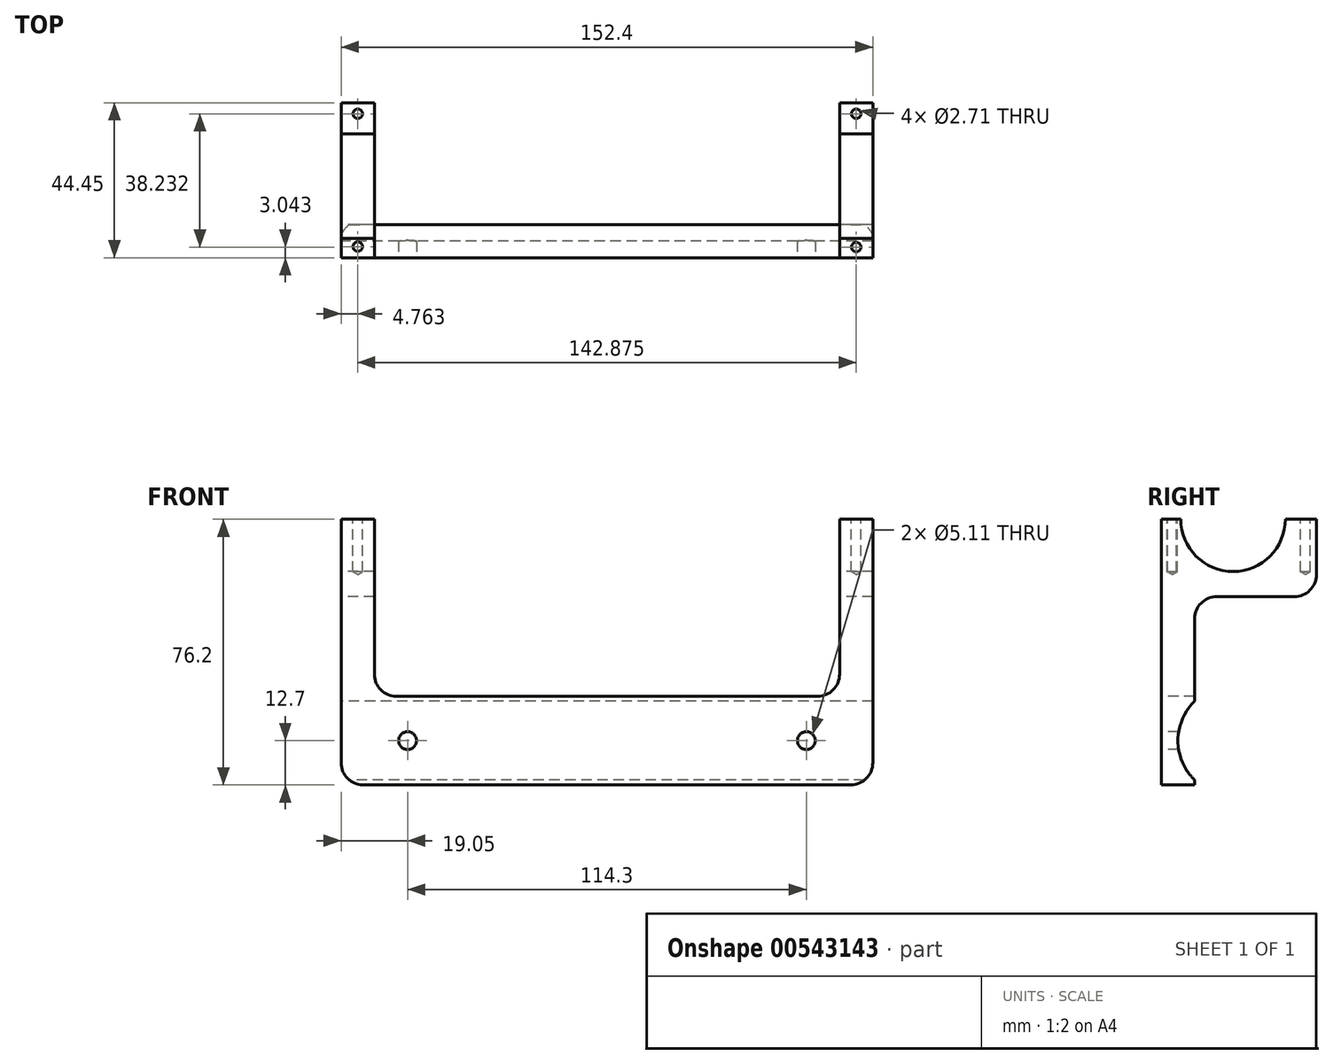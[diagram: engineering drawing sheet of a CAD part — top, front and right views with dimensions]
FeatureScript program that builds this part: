
annotation { "Feature Type Name" : "Feature", "Feature Type Description" : "" }
export const myFeature = defineFeature(function(context is Context, id is Id, definition is map)
    precondition{}
    {
        {
            var Q0;
            Q0=qCreatedBy(makeId("Right.planeOp"),FACE);
            var sketch = newSketch(context, id + "F0", { "sketchPlane" : qUnion([Q0])});
            skLineSegment(sketch, "E0.bottom", {"start": v(-44.45, 76.2) * mm, "end": v(0, 76.2) * mm, "construction": true});
            skLineSegment(sketch, "E0.top", {"start": v(-44.45, 0) * mm, "end": v(0, 0) * mm, "construction": true});
            skLineSegment(sketch, "E0.left", {"start": v(-44.45, 76.2) * mm, "end": v(-44.45, 0) * mm, "construction": true});
            skLineSegment(sketch, "E0.right", {"start": v(0, 76.2) * mm, "end": v(0, 0) * mm, "construction": true});
            skArc(sketch, "E1", {"start": v(-38.9, 76.2) * mm, "mid": v(-23.9, 61.2) * mm, "end": v(-8.9, 76.2) * mm});
            skLineSegment(sketch, "E2", {"start": v(-8.9, 76.2) * mm, "end": v(0, 76.2) * mm});
            skLineSegment(sketch, "E3", {"start": v(0, 53.98) * mm, "end": v(0, 76.2) * mm});
            skLineSegment(sketch, "E4", {"start": v(-38.9, 76.2) * mm, "end": v(-44.45, 76.2) * mm});
            skLineSegment(sketch, "E5", {"start": v(-44.45, 76.2) * mm, "end": v(-44.45, 0) * mm});
            skLineSegment(sketch, "E6", {"start": v(-44.45, 0) * mm, "end": v(-34.93, 0) * mm});
            skLineSegment(sketch, "E7", {"start": v(-34.93, 0) * mm, "end": v(-34.93, 53.98) * mm});
            skLineSegment(sketch, "E8", {"start": v(-34.93, 53.98) * mm, "end": v(0, 53.98) * mm});
            skArc(sketch, "E9", {"start": v(-34.93, 23.98) * mm, "mid": v(-39.69, 12.7) * mm, "end": v(-34.93, 1.42) * mm});
            skSolve(sketch);
        }
        {
            var Q0;
            Q0=makeQuery(id+"F0.imprint","IMPRINT",FACE,{"disambiguationData":[TD([[makeQuery(id+"F0.imprint","IMPRINT",EDGE,{"derivedFrom":sQuery(id+"F0.wireOp",EDGE,"E1")}),-1.0]])]});
            extrude(context, id + "F1", {"entities" : qUnion([Q0]), "depth" : 152.4 * mm, "offsetDistance" : 25.4 * mm});
        }
        {
            var Q0;
            Q0=makeQuery(id+"F1.opExtrude","SWEPT_FACE",FACE,{"disambiguationData":[OSD([sQuery(id+"F0.wireOp",EDGE,"E5")])]});
            var sketch = newSketch(context, id + "F2", { "sketchPlane" : qUnion([Q0])});
            skLineSegment(sketch, "E10.bottom", {"start": v(9.53, 76.2) * mm, "end": v(142.88, 76.2) * mm});
            skLineSegment(sketch, "E10.top", {"start": v(9.53, 25.4) * mm, "end": v(142.88, 25.4) * mm});
            skLineSegment(sketch, "E10.left", {"start": v(9.52, 76.2) * mm, "end": v(9.53, 25.4) * mm});
            skLineSegment(sketch, "E10.right", {"start": v(142.88, 76.2) * mm, "end": v(142.88, 25.4) * mm});
            skSolve(sketch);
        }
        {
            var Q0;
            Q0=makeQuery(id+"F2.imprint","IMPRINT",FACE,{"disambiguationData":[TD([[makeQuery(id+"F2.imprint","IMPRINT",EDGE,{"derivedFrom":sQuery(id+"F2.wireOp",EDGE,"E10.bottom")}),1.0]])]});
            extrude(context, id + "F3", {"entities" : qUnion([Q0]), "operationType" : NewBodyOperationType.REMOVE, "endBound" : BoundingType.THROUGH_ALL, "oppositeDirection" : true, "depth" : 25.4 * mm, "offsetDistance" : 25.4 * mm});
        }
        {
            var Q0;
            {var subQ0=sQuery(id+"F0.wireOp",EDGE,"E8");var subQ1=sQuery(id+"F0.wireOp",EDGE,"E3");Q0=makeQuery(id+"F3.boolean.opBoolean","SPLIT",EDGE,{"disambiguationData":[TD([makeQuery(id+"F3.opExtrude","SWEPT_FACE",FACE,{"disambiguationData":[OSD([sQuery(id+"F2.wireOp",EDGE,"E10.right")])]})])],"derivedFrom":makeQuery(id+"F1.opExtrude","SWEPT_EDGE",EDGE,{"disambiguationData":[OSD([subQ1,subQ0])]})});}
            var Q1;
            {var subQ0=sQuery(id+"F0.wireOp",EDGE,"E8");var subQ1=sQuery(id+"F0.wireOp",EDGE,"E3");Q1=makeQuery(id+"F3.boolean.opBoolean","SPLIT",EDGE,{"disambiguationData":[TD([makeQuery(id+"F3.opExtrude","SWEPT_FACE",FACE,{"disambiguationData":[OSD([sQuery(id+"F2.wireOp",EDGE,"E10.left")])]})])],"derivedFrom":makeQuery(id+"F1.opExtrude","SWEPT_EDGE",EDGE,{"disambiguationData":[OSD([subQ1,subQ0])]})});}
            var Q2;
            {var subQ0=sQuery(id+"F0.wireOp",EDGE,"E8");var subQ1=sQuery(id+"F0.wireOp",EDGE,"E7");Q2=makeQuery(id+"F3.boolean.opBoolean","SPLIT",EDGE,{"disambiguationData":[TD([makeQuery(id+"F3.opExtrude","SWEPT_FACE",FACE,{"disambiguationData":[OSD([sQuery(id+"F2.wireOp",EDGE,"E10.left")])]})])],"derivedFrom":makeQuery(id+"F1.opExtrude","SWEPT_EDGE",EDGE,{"disambiguationData":[OSD([subQ1,subQ0])]})});}
            var Q3;
            {var subQ0=sQuery(id+"F0.wireOp",EDGE,"E8");var subQ1=sQuery(id+"F0.wireOp",EDGE,"E7");Q3=makeQuery(id+"F3.boolean.opBoolean","SPLIT",EDGE,{"disambiguationData":[TD([makeQuery(id+"F3.opExtrude","SWEPT_FACE",FACE,{"disambiguationData":[OSD([sQuery(id+"F2.wireOp",EDGE,"E10.right")])]})])],"derivedFrom":makeQuery(id+"F1.opExtrude","SWEPT_EDGE",EDGE,{"disambiguationData":[OSD([subQ1,subQ0])]})});}
            var Q4;
            Q4=makeQuery(id+"F1.opExtrude","CAP_EDGE",EDGE,{"disambiguationData":[OSD([sQuery(id+"F0.wireOp",EDGE,"E6")])],"isStart":false});
            var Q5;
            Q5=makeQuery(id+"F1.opExtrude","CAP_EDGE",EDGE,{"disambiguationData":[OSD([sQuery(id+"F0.wireOp",EDGE,"E6")])],"isStart":true});
            var Q6;
            Q6=makeQuery(id+"F3.boolean.opBoolean","COPY",EDGE,{"derivedFrom":makeQuery(id+"F3.opExtrude","SWEPT_EDGE",EDGE,{"disambiguationData":[OSD([sQuery(id+"F2.wireOp",EDGE,"E10.top"),sQuery(id+"F2.wireOp",EDGE,"E10.right")])]})});
            var Q7;
            Q7=makeQuery(id+"F3.boolean.opBoolean","COPY",EDGE,{"derivedFrom":makeQuery(id+"F3.opExtrude","SWEPT_EDGE",EDGE,{"disambiguationData":[OSD([sQuery(id+"F2.wireOp",EDGE,"E10.top"),sQuery(id+"F2.wireOp",EDGE,"E10.left")])]})});
            fillet(context, id + "F4", {"entities" : qUnion([Q0, Q1, Q2, Q3, Q4, Q5, Q6, Q7]), "radius" : 6.35 * mm, "tangentPropagation" : true, "allowEdgeOverflow" : false});
        }
        {
            var Q0;
            Q0=makeQuery(id+"F1.opExtrude","SWEPT_FACE",FACE,{"disambiguationData":[OSD([sQuery(id+"F0.wireOp",EDGE,"E5")])]});
            var sketch = newSketch(context, id + "F5", { "sketchPlane" : qUnion([Q0])});
            skPoint(sketch, "E11", {"position": v(19.05, 12.7) * mm});
            skPoint(sketch, "E12", {"position": v(133.35, 12.7) * mm});
            skSolve(sketch);
        }
        {
            var Q0;
            Q0=sQuery(id+"F5.wireOp",VERTEX,"E11");
            var Q1;
            Q1=sQuery(id+"F5.wireOp",VERTEX,"E12");
            var Q2;
            Q2=makeQuery(id+"F1.opExtrude","SWEPT_BODY",BODY,{"disambiguationData":[OSD([sQuery(id+"F0.wireOp",EDGE,"E1"),sQuery(id+"F0.wireOp",EDGE,"E2"),sQuery(id+"F0.wireOp",EDGE,"E3"),sQuery(id+"F0.wireOp",EDGE,"E4"),sQuery(id+"F0.wireOp",EDGE,"E5"),sQuery(id+"F0.wireOp",EDGE,"E6"),sQuery(id+"F0.wireOp",EDGE,"E7"),sQuery(id+"F0.wireOp",EDGE,"E8")])]});
            hole(context, id + "F6", {"style" : HoleStyle.SIMPLE, "endStyle" : HoleEndStyle.THROUGH, "standardTappedOrClearance" : lookupTablePath({ "standard" : "ANSI", "fit" : "Normal (ASME)", "size" : "#10", "type" : "Clearance" }), "standardBlindInLast" : lookupTablePath({ "fit" : "Free", "standard" : "ANSI", "size" : "#10", "type" : "Clearance" }), "holeDiameter" : 5.1 * mm, "isTappedThrough" : true, "tappedDepth" : 12.7 * mm, "tapClearance" : 3, "locations" : qUnion([Q0, Q1]), "scope" : qUnion([Q2])});
        }
        {
            var Q0;
            {var subQ2=sQuery(id+"F0.wireOp",EDGE,"E4");Q0=makeQuery(id+"F3.boolean.opBoolean","SPLIT",FACE,{"disambiguationData":[TD([makeQuery(id+"F3.opExtrude","SWEPT_FACE",FACE,{"disambiguationData":[OSD([sQuery(id+"F2.wireOp",EDGE,"E10.right")])]})])],"derivedFrom":makeQuery(id+"F1.opExtrude","SWEPT_FACE",FACE,{"disambiguationData":[OSD([subQ2])]})});}
            var sketch = newSketch(context, id + "F7", { "sketchPlane" : qUnion([Q0])});
            skPoint(sketch, "E13", {"position": v(4.76, -3.18) * mm});
            skPoint(sketch, "E14", {"position": v(4.76, -41.28) * mm});
            skPoint(sketch, "E15", {"position": v(147.64, -3.18) * mm});
            skPoint(sketch, "E16", {"position": v(147.64, -41.4) * mm});
            skSolve(sketch);
        }
        {
            var Q0;
            Q0=sQuery(id+"F7.wireOp",VERTEX,"E13");
            var Q1;
            Q1=sQuery(id+"F7.wireOp",VERTEX,"E14");
            var Q2;
            Q2=sQuery(id+"F7.wireOp",VERTEX,"E15");
            var Q3;
            Q3=sQuery(id+"F7.wireOp",VERTEX,"E16");
            var Q4;
            Q4=makeQuery(id+"F1.opExtrude","SWEPT_BODY",BODY,{"disambiguationData":[OSD([sQuery(id+"F0.wireOp",EDGE,"E1"),sQuery(id+"F0.wireOp",EDGE,"E2"),sQuery(id+"F0.wireOp",EDGE,"E3"),sQuery(id+"F0.wireOp",EDGE,"E4"),sQuery(id+"F0.wireOp",EDGE,"E5"),sQuery(id+"F0.wireOp",EDGE,"E6"),sQuery(id+"F0.wireOp",EDGE,"E7"),sQuery(id+"F0.wireOp",EDGE,"E8")])]});
            hole(context, id + "F8", {"style" : HoleStyle.SIMPLE, "endStyle" : HoleEndStyle.BLIND, "standardTappedOrClearance" : lookupTablePath({ "standard" : "ANSI", "engagement" : "75%", "pitch" : "32 tpi", "size" : "#6", "type" : "Tapped" }), "standardBlindInLast" : lookupTablePath({ "standard" : "ANSI", "engagement" : "75%", "pitch" : "32 tpi", "size" : "#6", "type" : "Tapped" }), "holeDiameter" : 2.7 * mm, "showTappedDepth" : true, "holeDepth" : 15.08 * mm, "isTappedThrough" : true, "tappedDepth" : 12.7 * mm, "tapClearance" : 3, "locations" : qUnion([Q0, Q1, Q2, Q3]), "scope" : qUnion([Q4]), "majorDiameter" : 3.5 * mm});
        }
    });
